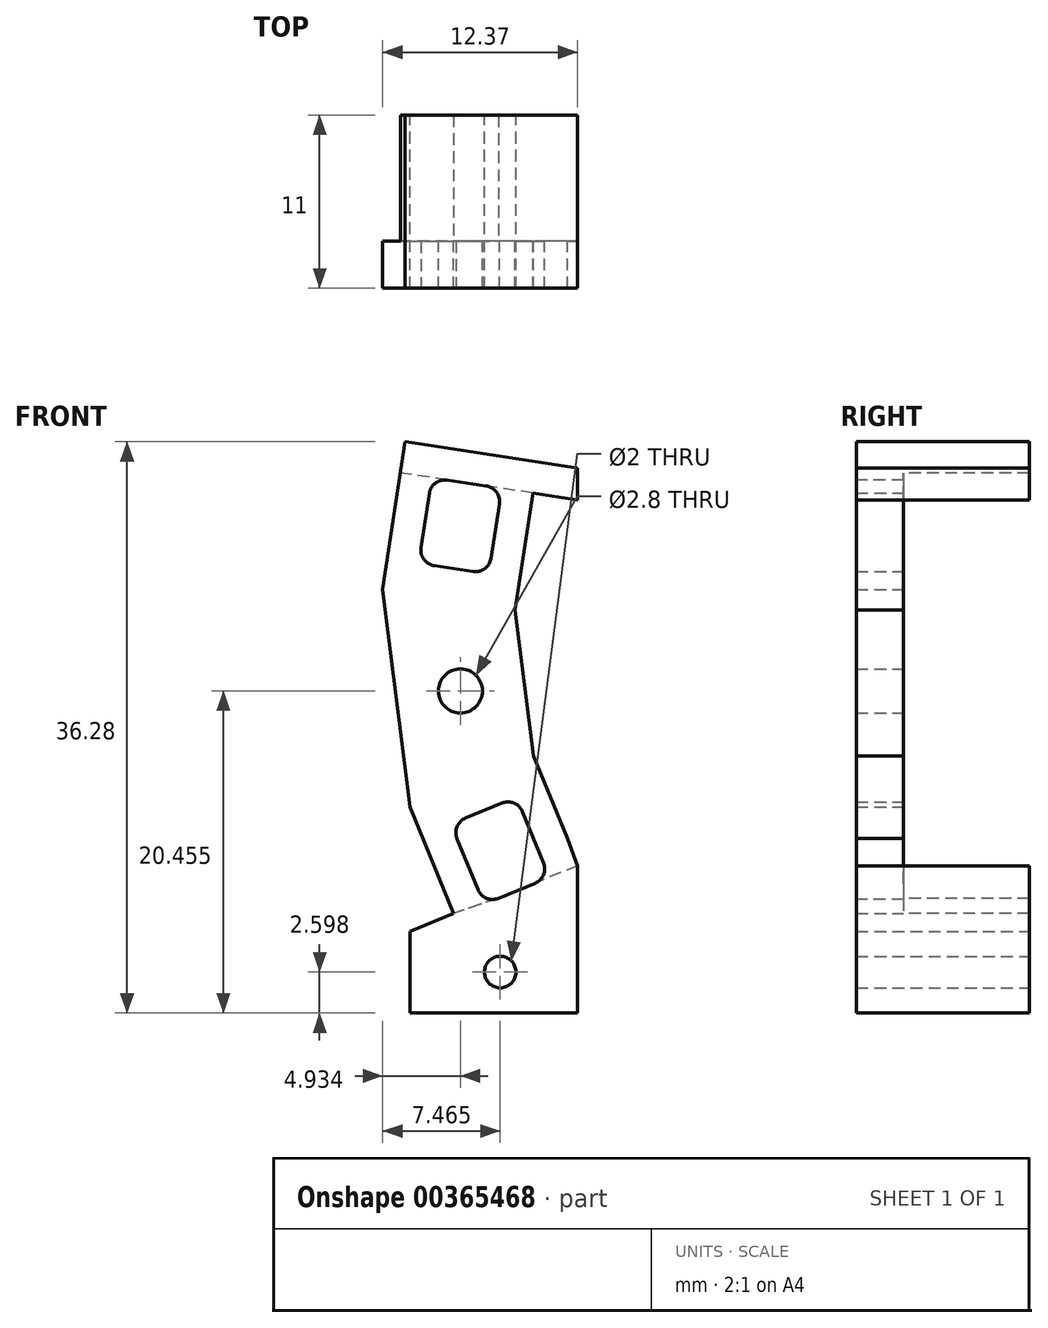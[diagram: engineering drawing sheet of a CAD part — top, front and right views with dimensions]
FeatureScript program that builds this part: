
annotation { "Feature Type Name" : "Feature", "Feature Type Description" : "" }
export const myFeature = defineFeature(function(context is Context, id is Id, definition is map)
    precondition{}
    {
        {
            var Q0;
            Q0=qCreatedBy(makeId("Front.planeOp"),FACE);
            var sketch = newSketch(context, id + "F0", { "sketchPlane" : qUnion([Q0])});
            skLineSegment(sketch, "E0", {"start": v(62.96, -34.45) * mm, "end": v(66.2, -33.12) * mm});
            skLineSegment(sketch, "E1", {"start": v(64.11, -28.03) * mm, "end": v(60.87, -29.37) * mm});
            skLineSegment(sketch, "E2.1", {"start": v(67.35, -30.65) * mm, "end": v(66.66, -28.99) * mm});
            skLineSegment(sketch, "E2.3", {"start": v(57.34, -28.66) * mm, "end": v(60.11, -35.4) * mm});
            skLineSegment(sketch, "E3.trimOffspring", {"start": v(67.98, -41.74) * mm, "end": v(57.34, -41.74) * mm});
            skLineSegment(sketch, "E4.trimOffspring", {"start": v(57.34, -36.55) * mm, "end": v(57.34, -41.74) * mm});
            skLineSegment(sketch, "E5.trimOffspring", {"start": v(60.11, -35.4) * mm, "end": v(57.34, -36.55) * mm});
            skCircle(sketch, "E6", {"center": v(63.07, -39.14) * mm, "radius": 1 * mm});
            skPoint(sketch, "E6.centerSnap0", {"position": v(57.34, -39.14) * mm});
            skPoint(sketch, "E6.centerSnap1", {"position": v(63.07, -41.74) * mm});
            skLineSegment(sketch, "E7", {"start": v(60.95, -8.08) * mm, "end": v(59.7, -7.89) * mm});
            skLineSegment(sketch, "E8", {"start": v(58.88, -13.33) * mm, "end": v(62.34, -13.85) * mm});
            skLineSegment(sketch, "E9", {"start": v(63.17, -8.42) * mm, "end": v(60.95, -8.08) * mm});
            skLineSegment(sketch, "E10.0", {"start": v(57.04, -5.46) * mm, "end": v(55.61, -14.85) * mm});
            skLineSegment(sketch, "E10.1", {"start": v(61.25, -6.1) * mm, "end": v(57.04, -5.46) * mm});
            skLineSegment(sketch, "E10.3", {"start": v(64.02, -16.13) * mm, "end": v(64.32, -14.15) * mm});
            skLineSegment(sketch, "E10.4", {"start": v(65.45, -6.74) * mm, "end": v(61.25, -6.1) * mm});
            skLineSegment(sketch, "E11", {"start": v(55.61, -14.85) * mm, "end": v(57.34, -28.66) * mm});
            skPoint(sketch, "E12.endSnap0", {"position": v(69.62, -9.4) * mm});
            skLineSegment(sketch, "E13", {"start": v(65.45, -6.74) * mm, "end": v(67.98, -7.13) * mm});
            skPoint(sketch, "E14.orphan", {"position": v(69.62, -5.2) * mm});
            skLineSegment(sketch, "E15", {"start": v(67.98, -32.4) * mm, "end": v(67.98, -41.74) * mm});
            skPoint(sketch, "E16.orphan", {"position": v(68.81, -41.74) * mm});
            skLineSegment(sketch, "E17.trimOffspring", {"start": v(67.98, -9.15) * mm, "end": v(67.98, -7.13) * mm});
            skLineSegment(sketch, "E18", {"start": v(64.02, -16.13) * mm, "end": v(65.2, -25.42) * mm});
            skLineSegment(sketch, "E19.trimOffspring", {"start": v(65.15, -8.72) * mm, "end": v(67.98, -9.15) * mm});
            skCircle(sketch, "E20", {"center": v(60.54, -21.29) * mm, "radius": 1.4 * mm});
            skLineSegment(sketch, "E21.trimOffspring", {"start": v(64.6, -12.33) * mm, "end": v(64.87, -10.55) * mm});
            skPoint(sketch, "E22.orphan", {"position": v(62.76, -11.13) * mm});
            skPoint(sketch, "E23.orphan", {"position": v(58.72, -7.74) * mm});
            skPoint(sketch, "E24.orphan", {"position": v(57.9, -13.18) * mm});
            skPoint(sketch, "E25.start.orphan", {"position": v(58.3, -10.46) * mm});
            skLineSegment(sketch, "E26.trimOffspring", {"start": v(65.96, -27.27) * mm, "end": v(65.2, -25.42) * mm});
            skPoint(sketch, "E27.orphan", {"position": v(59.95, -29.75) * mm});
            skPoint(sketch, "E28.orphan", {"position": v(62.04, -34.83) * mm});
            skPoint(sketch, "E29.start.orphan", {"position": v(61, -32.29) * mm});
            skLineSegment(sketch, "E30", {"start": v(59.7, -7.89) * mm, "end": v(58.72, -7.74) * mm});
            skLineSegment(sketch, "E31", {"start": v(58.72, -7.74) * mm, "end": v(57.9, -13.18) * mm});
            skLineSegment(sketch, "E32", {"start": v(63.17, -8.42) * mm, "end": v(62.34, -13.85) * mm});
            skLineSegment(sketch, "E33", {"start": v(57.9, -13.18) * mm, "end": v(58.88, -13.33) * mm});
            skLineSegment(sketch, "E34", {"start": v(65.15, -8.72) * mm, "end": v(64.32, -14.15) * mm});
            skLineSegment(sketch, "E35", {"start": v(64.11, -28.03) * mm, "end": v(66.2, -33.12) * mm});
            skLineSegment(sketch, "E36", {"start": v(59.95, -29.75) * mm, "end": v(62.04, -34.83) * mm});
            skLineSegment(sketch, "E37", {"start": v(62.96, -34.45) * mm, "end": v(62.04, -34.83) * mm});
            skLineSegment(sketch, "E38", {"start": v(60.87, -29.37) * mm, "end": v(59.95, -29.75) * mm});
            skLineSegment(sketch, "E39", {"start": v(65.96, -27.27) * mm, "end": v(67.35, -30.65) * mm});
            skLineSegment(sketch, "E40", {"start": v(67.35, -30.65) * mm, "end": v(67.98, -32.4) * mm});
            skSolve(sketch);
        }
        {
            var Q0;
            Q0 = qSketchRegion(id + "F0", true);
            extrude(context, id + "F1", {"entities" : qUnion([Q0]), "depth" : 3 * mm});
        }
        {
            var Q0;
            Q0=makeQuery(id+"F1.opExtrude","SWEPT_EDGE",EDGE,{"disambiguationData":[OSD([sQuery(id+"F0.wireOp",EDGE,"E9"),sQuery(id+"F0.wireOp",EDGE,"E32")])]});
            var Q1;
            Q1=makeQuery(id+"F1.opExtrude","SWEPT_EDGE",EDGE,{"disambiguationData":[OSD([sQuery(id+"F0.wireOp",EDGE,"E31"),sQuery(id+"F0.wireOp",EDGE,"E33")])]});
            var Q2;
            Q2=makeQuery(id+"F1.opExtrude","SWEPT_EDGE",EDGE,{"disambiguationData":[OSD([sQuery(id+"F0.wireOp",EDGE,"E30"),sQuery(id+"F0.wireOp",EDGE,"E31")])]});
            var Q3;
            Q3=makeQuery(id+"F1.opExtrude","SWEPT_EDGE",EDGE,{"disambiguationData":[OSD([sQuery(id+"F0.wireOp",EDGE,"E8"),sQuery(id+"F0.wireOp",EDGE,"E32")])]});
            var Q4;
            Q4=makeQuery(id+"F1.opExtrude","SWEPT_EDGE",EDGE,{"disambiguationData":[OSD([sQuery(id+"F0.wireOp",EDGE,"E1"),sQuery(id+"F0.wireOp",EDGE,"E35")])]});
            var Q5;
            Q5=makeQuery(id+"F1.opExtrude","SWEPT_EDGE",EDGE,{"disambiguationData":[OSD([sQuery(id+"F0.wireOp",EDGE,"E36"),sQuery(id+"F0.wireOp",EDGE,"E38")])]});
            var Q6;
            Q6=makeQuery(id+"F1.opExtrude","SWEPT_EDGE",EDGE,{"disambiguationData":[OSD([sQuery(id+"F0.wireOp",EDGE,"E0"),sQuery(id+"F0.wireOp",EDGE,"E35")])]});
            var Q7;
            Q7=makeQuery(id+"F1.opExtrude","SWEPT_EDGE",EDGE,{"disambiguationData":[OSD([sQuery(id+"F0.wireOp",EDGE,"E36"),sQuery(id+"F0.wireOp",EDGE,"E37")])]});
            fillet(context, id + "F2", {"entities" : qUnion([Q0, Q1, Q2, Q3, Q4, Q5, Q6, Q7]), "radius" : 1 * mm, "tangentPropagation" : true, "allowEdgeOverflow" : false});
        }
        {
            var Q0;
            Q0=makeQuery(id+"F1.opExtrude","CAP_FACE",FACE,{"disambiguationData":[OSD([sQuery(id+"F0.wireOp",EDGE,"E0"),sQuery(id+"F0.wireOp",EDGE,"E1"),sQuery(id+"F0.wireOp",EDGE,"E2.3"),sQuery(id+"F0.wireOp",EDGE,"E3.trimOffspring"),sQuery(id+"F0.wireOp",EDGE,"E4.trimOffspring"),sQuery(id+"F0.wireOp",EDGE,"E5.trimOffspring"),sQuery(id+"F0.wireOp",EDGE,"E6"),sQuery(id+"F0.wireOp",EDGE,"E7"),sQuery(id+"F0.wireOp",EDGE,"E8"),sQuery(id+"F0.wireOp",EDGE,"E9"),sQuery(id+"F0.wireOp",EDGE,"E10.0"),sQuery(id+"F0.wireOp",EDGE,"E10.1"),sQuery(id+"F0.wireOp",EDGE,"E10.3"),sQuery(id+"F0.wireOp",EDGE,"E10.4"),sQuery(id+"F0.wireOp",EDGE,"E11"),sQuery(id+"F0.wireOp",EDGE,"E13"),sQuery(id+"F0.wireOp",EDGE,"E15"),sQuery(id+"F0.wireOp",EDGE,"E17.trimOffspring"),sQuery(id+"F0.wireOp",EDGE,"E18"),sQuery(id+"F0.wireOp",EDGE,"E19.trimOffspring"),sQuery(id+"F0.wireOp",EDGE,"E20"),sQuery(id+"F0.wireOp",EDGE,"E26.trimOffspring"),sQuery(id+"F0.wireOp",EDGE,"E30"),sQuery(id+"F0.wireOp",EDGE,"E31"),sQuery(id+"F0.wireOp",EDGE,"E32"),sQuery(id+"F0.wireOp",EDGE,"E33"),sQuery(id+"F0.wireOp",EDGE,"E34"),sQuery(id+"F0.wireOp",EDGE,"E35"),sQuery(id+"F0.wireOp",EDGE,"E36"),sQuery(id+"F0.wireOp",EDGE,"E37"),sQuery(id+"F0.wireOp",EDGE,"E38"),sQuery(id+"F0.wireOp",EDGE,"E39"),sQuery(id+"F0.wireOp",EDGE,"E40")])],"isStart":true});
            var sketch = newSketch(context, id + "F3", { "sketchPlane" : qUnion([Q0])});
            skLineSegment(sketch, "E41", {"start": v(-67.98, -32.4) * mm, "end": v(-62.96, -34.45) * mm});
            skLineSegment(sketch, "E42", {"start": v(-62.96, -34.45) * mm, "end": v(-60.11, -35.4) * mm});
            skLineSegment(sketch, "E43", {"start": v(-60.11, -35.4) * mm, "end": v(-57.34, -36.55) * mm});
            skLineSegment(sketch, "E44", {"start": v(-57.34, -36.55) * mm, "end": v(-57.34, -41.74) * mm});
            skLineSegment(sketch, "E45", {"start": v(-57.34, -41.74) * mm, "end": v(-67.98, -41.74) * mm});
            skLineSegment(sketch, "E46", {"start": v(-67.98, -41.74) * mm, "end": v(-67.98, -32.4) * mm});
            skCircle(sketch, "E47", {"center": v(-63.07, -39.14) * mm, "radius": 1 * mm});
            skLineSegment(sketch, "E48", {"start": v(-67.98, -7.13) * mm, "end": v(-67.98, -9.15) * mm});
            skLineSegment(sketch, "E49", {"start": v(-67.98, -9.15) * mm, "end": v(-56.74, -7.44) * mm});
            skLineSegment(sketch, "E50", {"start": v(-67.98, -7.13) * mm, "end": v(-57.04, -5.46) * mm});
            skLineSegment(sketch, "E51", {"start": v(-57.04, -5.46) * mm, "end": v(-56.74, -7.44) * mm});
            skSolve(sketch);
        }
        {
            var Q0;
            Q0 = qSketchRegion(id + "F3", true);
            extrude(context, id + "F4", {"entities" : qUnion([Q0]), "operationType" : NewBodyOperationType.ADD, "depth" : 8 * mm});
        }
    });
